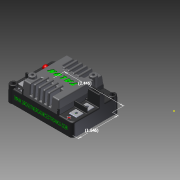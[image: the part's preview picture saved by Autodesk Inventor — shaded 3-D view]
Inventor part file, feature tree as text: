
AUTODESK INVENTOR PART (.ipt)
format: ipt  version: 2015 SP1 (Build 190203100, 203)  size: 4,907,520 bytes
history: native  units: in
note: dims shown in document units (in); Inventor stores cm internally (conversion verified against a paired STEP export)
features: other x19, imported_body x18, plane x1, sketch x1
ambient origin geometry x8: Origin, YZ Plane, XZ Plane, XY Plane, X Axis, Y Axis, Z Axis, Center Point
bodies: Body1 (feature_tree), Body2 (feature_tree), Body3 (feature_tree), Body4 (feature_tree), Body5 (feature_tree), Body6 (feature_tree), Body7 (feature_tree), Body8 (feature_tree), Body9 (feature_tree), Body10 (feature_tree), Body11 (feature_tree), Body12 (feature_tree), Body13 (feature_tree), Body14 (feature_tree), Body15 (feature_tree), Body16 (feature_tree), Body17 (feature_tree), Body18 (feature_tree)
feature tree (39):
  parser-record x1  (decoder bookkeeping rows leaked as tree rows — omitted from the tree; the rows remain in map.json)
  other  "Talon1"
  plane  "Work Plane1"
  sketch  "Sketch1"  dims[d0=90.0deg d1=2.446in d2=1.646in]
  other  "NONE_1"
  other  "NONE_2"
  other  "NONE_3"
  other  "NONE_4"
  other  "NONE_5"
  other  "NONE_6"
  other  "NONE_7"
  other  "NONE_8"
  other  "NONE_9"
  other  "NONE_10"
  other  "NONE_11"
  other  "NONE_12"
  other  "NONE_13"
  other  "NONE_14"
  other  "NONE_15"
  other  "NONE_16"
  other  "NONE_17"
  imported_body  "Base1"
  imported_body  "Base2"
  imported_body  "Base3"
  imported_body  "Base4"
  imported_body  "Base5"
  imported_body  "Base6"
  imported_body  "Base7"
  imported_body  "Base8"
  imported_body  "Base9"
  imported_body  "Base10"
  imported_body  "Base11"
  imported_body  "Base12"
  imported_body  "Base13"
  imported_body  "Base14"
  imported_body  "Base15"
  imported_body  "Base16"
  imported_body  "Base17"
  imported_body  "Base18"
